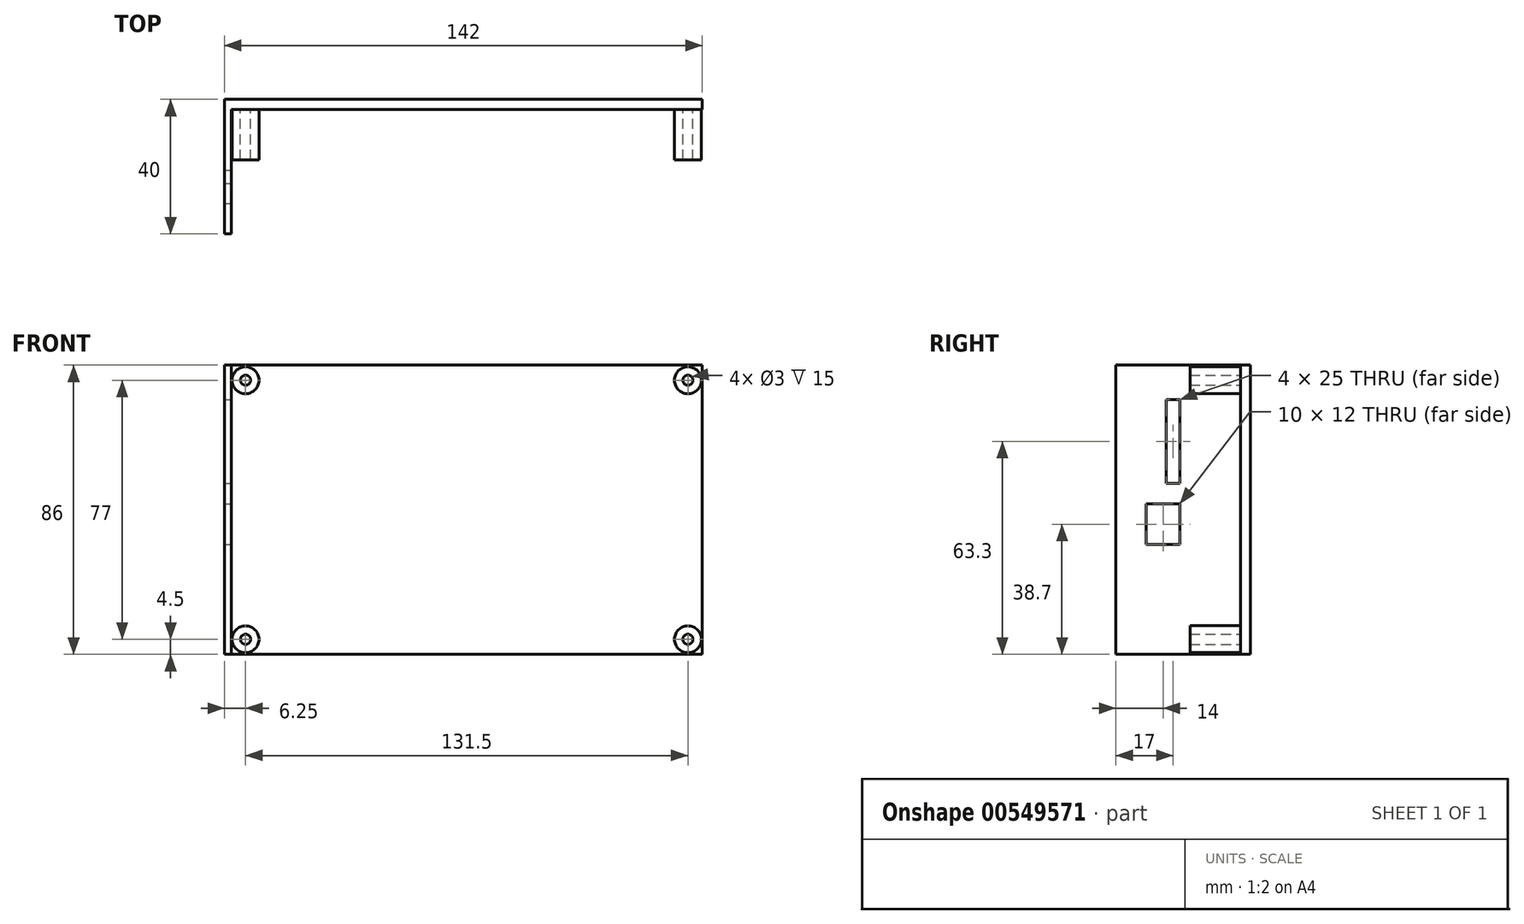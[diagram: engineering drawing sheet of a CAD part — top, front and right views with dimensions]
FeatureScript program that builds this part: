
annotation { "Feature Type Name" : "Feature", "Feature Type Description" : "" }
export const myFeature = defineFeature(function(context is Context, id is Id, definition is map)
    precondition{}
    {
        {
            var Q0;
            Q0=qCreatedBy(makeId("Front.planeOp"),FACE);
            var sketch = newSketch(context, id + "F0", { "sketchPlane" : qUnion([Q0])});
            skLineSegment(sketch, "E0.bottom", {"start": v(-70, 43) * mm, "end": v(70, 43) * mm});
            skLineSegment(sketch, "E0.top", {"start": v(-70, -43) * mm, "end": v(70, -43) * mm});
            skLineSegment(sketch, "E0.left", {"start": v(-70, 43) * mm, "end": v(-70, -43) * mm});
            skLineSegment(sketch, "E0.right", {"start": v(70, 43) * mm, "end": v(70, -43) * mm});
            skSolve(sketch);
        }
        {
            var Q0;
            Q0 = qSketchRegion(id + "F0", true);
            extrude(context, id + "F1", {"entities" : qUnion([Q0]), "oppositeDirection" : true, "depth" : 3 * mm, "offsetDistance" : 25 * mm});
        }
        {
            var Q0;
            Q0=makeQuery(id+"F1.opExtrude","CAP_FACE",FACE,{"disambiguationData":[OSD([sQuery(id+"F0.wireOp",EDGE,"E0.bottom"),sQuery(id+"F0.wireOp",EDGE,"E0.top"),sQuery(id+"F0.wireOp",EDGE,"E0.left"),sQuery(id+"F0.wireOp",EDGE,"E0.right")])],"isStart":true});
            var sketch = newSketch(context, id + "F2", { "sketchPlane" : qUnion([Q0])});
            skLineSegment(sketch, "E1.bottom", {"start": v(-65.75, 38.5) * mm, "end": v(65.75, 38.5) * mm, "construction": true});
            skLineSegment(sketch, "E1.top", {"start": v(-65.75, -38.5) * mm, "end": v(65.75, -38.5) * mm, "construction": true});
            skLineSegment(sketch, "E1.left", {"start": v(-65.75, 38.5) * mm, "end": v(-65.75, -38.5) * mm, "construction": true});
            skLineSegment(sketch, "E1.right", {"start": v(65.75, 38.5) * mm, "end": v(65.75, -38.5) * mm, "construction": true});
            skCircle(sketch, "E2", {"center": v(-65.75, 38.5) * mm, "radius": 1.5 * mm});
            skCircle(sketch, "E3", {"center": v(65.75, 38.5) * mm, "radius": 1.5 * mm});
            skCircle(sketch, "E4", {"center": v(65.75, 38.5) * mm, "radius": 4 * mm});
            skCircle(sketch, "E5", {"center": v(-65.75, 38.5) * mm, "radius": 4 * mm});
            skCircle(sketch, "E6", {"center": v(-65.75, -38.5) * mm, "radius": 1.5 * mm});
            skCircle(sketch, "E7", {"center": v(-65.75, -38.5) * mm, "radius": 4 * mm});
            skCircle(sketch, "E8", {"center": v(65.75, -38.5) * mm, "radius": 4 * mm});
            skCircle(sketch, "E9", {"center": v(65.75, -38.5) * mm, "radius": 1.5 * mm});
            skSolve(sketch);
        }
        {
            var Q0;
            Q0 = qSketchRegion(id + "F2", true);
            extrude(context, id + "F3", {"entities" : qUnion([Q0]), "operationType" : NewBodyOperationType.ADD, "depth" : 15 * mm, "offsetDistance" : 25 * mm});
        }
        {
            var Q0;
            Q0=makeQuery(id+"F1.opExtrude","SWEPT_FACE",FACE,{"disambiguationData":[OSD([sQuery(id+"F0.wireOp",EDGE,"E0.left")])]});
            var sketch = newSketch(context, id + "F4", { "sketchPlane" : qUnion([Q0])});
            skLineSegment(sketch, "E10.bottom", {"start": v(-3, 43) * mm, "end": v(37, 43) * mm});
            skLineSegment(sketch, "E10.top", {"start": v(-3, -43) * mm, "end": v(37, -43) * mm});
            skLineSegment(sketch, "E10.left", {"start": v(-3, 43) * mm, "end": v(-3, -43) * mm});
            skLineSegment(sketch, "E10.right", {"start": v(37, 43) * mm, "end": v(37, -43) * mm});
            skLineSegment(sketch, "E11.bottom", {"start": v(18, 32.8) * mm, "end": v(22, 32.8) * mm});
            skLineSegment(sketch, "E11.top", {"start": v(18, 7.8) * mm, "end": v(22, 7.8) * mm});
            skLineSegment(sketch, "E11.left", {"start": v(18, 32.8) * mm, "end": v(18, 7.8) * mm});
            skLineSegment(sketch, "E11.right", {"start": v(22, 32.8) * mm, "end": v(22, 7.8) * mm});
            skLineSegment(sketch, "E12.left", {"start": v(18, 1.7) * mm, "end": v(18, -10.3) * mm});
            skLineSegment(sketch, "E13", {"start": v(18, 1.7) * mm, "end": v(28, 1.7) * mm});
            skLineSegment(sketch, "E14", {"start": v(28, 1.7) * mm, "end": v(28, -10.3) * mm});
            skLineSegment(sketch, "E15", {"start": v(28, -10.3) * mm, "end": v(18, -10.3) * mm});
            skSolve(sketch);
        }
        {
            var Q0;
            Q0 = qSketchRegion(id + "F4", true);
            extrude(context, id + "F5", {"entities" : qUnion([Q0]), "operationType" : NewBodyOperationType.ADD, "depth" : 2 * mm, "offsetDistance" : 25 * mm});
        }
    });
